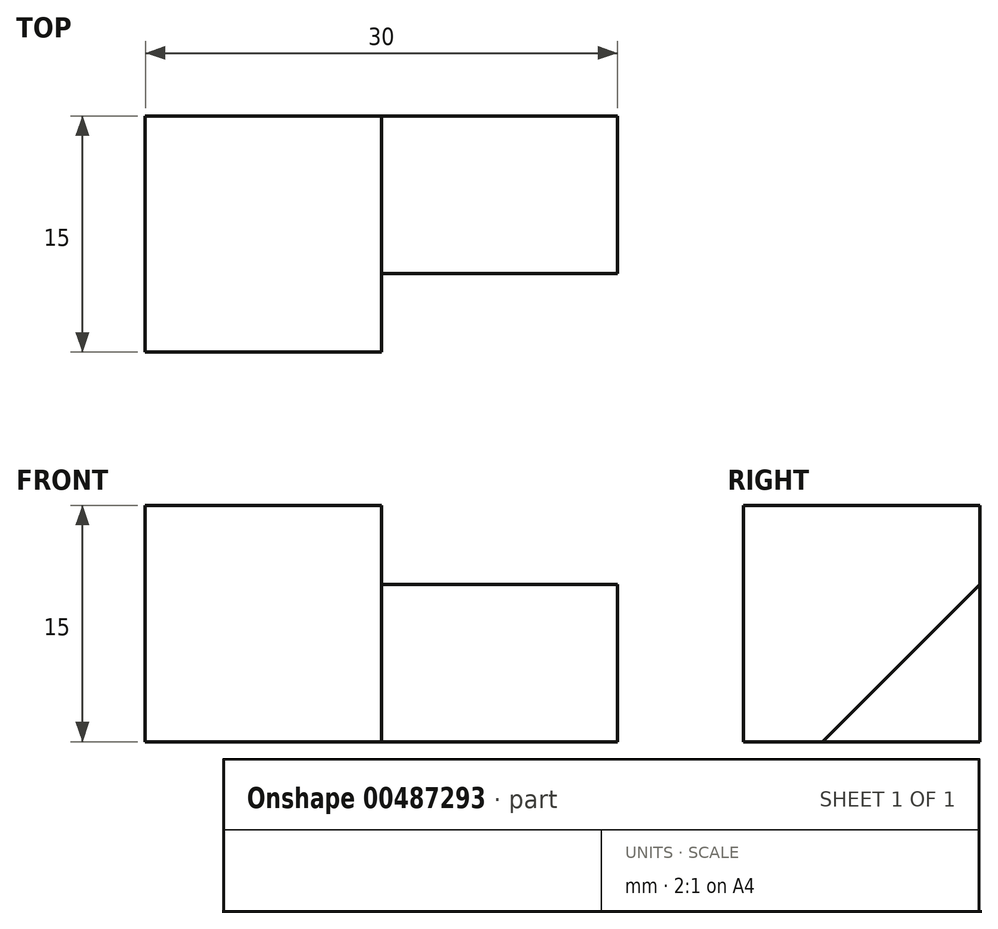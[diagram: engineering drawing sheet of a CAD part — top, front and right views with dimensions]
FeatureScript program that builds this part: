
annotation { "Feature Type Name" : "Feature", "Feature Type Description" : "" }
export const myFeature = defineFeature(function(context is Context, id is Id, definition is map)
    precondition{}
    {
        {
            var Q0;
            Q0=qCreatedBy(makeId("Top.planeOp"),FACE);
            var sketch = newSketch(context, id + "F0", { "sketchPlane" : qUnion([Q0])});
            skLineSegment(sketch, "E0.bottom", {"start": v(-4.6, 11.33) * mm, "end": v(10.4, 11.33) * mm});
            skLineSegment(sketch, "E0.top", {"start": v(-4.6, -3.67) * mm, "end": v(10.4, -3.67) * mm});
            skLineSegment(sketch, "E0.left", {"start": v(-4.6, 11.33) * mm, "end": v(-4.6, -3.67) * mm});
            skLineSegment(sketch, "E0.right", {"start": v(10.4, 11.33) * mm, "end": v(10.4, -3.67) * mm});
            skSolve(sketch);
        }
        {
            var Q0;
            Q0=makeQuery(id+"F0.imprint","IMPRINT",FACE,{"disambiguationData":[TD([[makeQuery(id+"F0.imprint","IMPRINT",EDGE,{"derivedFrom":sQuery(id+"F0.wireOp",EDGE,"E0.bottom")}),-1.0]])]});
            extrude(context, id + "F1", {"entities" : qUnion([Q0]), "depth" : 15 * mm});
        }
        {
            var Q0;
            Q0=makeQuery(id+"F1.opExtrude","SWEPT_FACE",FACE,{"disambiguationData":[OSD([sQuery(id+"F0.wireOp",EDGE,"E0.right")])]});
            var sketch = newSketch(context, id + "F2", { "sketchPlane" : qUnion([Q0])});
            skLineSegment(sketch, "E1", {"start": v(1.33, 0) * mm, "end": v(11.33, 10) * mm});
            skLineSegment(sketch, "E2", {"start": v(11.33, 10) * mm, "end": v(11.33, 0) * mm});
            skLineSegment(sketch, "E3", {"start": v(11.33, 0) * mm, "end": v(1.33, 0) * mm});
            skLineSegment(sketch, "E4", {"start": v(1.33, 0) * mm, "end": v(11.33, 0) * mm});
            skSolve(sketch);
        }
        {
            var Q0;
            Q0=makeQuery(id+"F2.imprint","IMPRINT",FACE,{"disambiguationData":[TD([[makeQuery(id+"F2.imprint","IMPRINT",EDGE,{"derivedFrom":sQuery(id+"F2.wireOp",EDGE,"E1")}),-1.0]])]});
            extrude(context, id + "F3", {"entities" : qUnion([Q0]), "operationType" : NewBodyOperationType.ADD, "depth" : 15 * mm});
        }
    });
